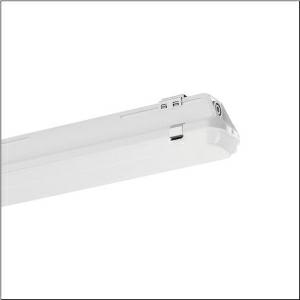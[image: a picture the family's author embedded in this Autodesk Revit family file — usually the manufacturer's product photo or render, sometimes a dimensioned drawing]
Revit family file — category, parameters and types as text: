
# Revit family: monsun_r__21_51fb207p660c005_979b
name_source: partatom
category: Lighting Fixtures
units: mm (PartAtom-declared; Revit-internal decimal feet)

## family parameters
Cut with Voids When Loaded = No
Host = Face
Light Source = No
Part Type = Normal
Room Calculation Point = No
Round Connector Dimension = Use Diameter
Shared = No

## types (1)
- Monsun® 21 (1 x LED, 5410 lm, 34.9 W, 6500K)
    Apparent Load = 35 VA
    CIE Flux Codes = 45 75 93 94 100
    Color Rendering = 80
    Color Temperature = 6500K
    Default Elevation = 1800 mm
    Description = Monsun® 21, damp-proof luminaire, chain hanger, primary optical cover: enclosure, of PC, light emission: direct distribution, primary light characteristic: symmetric, installation type: suspended mounting, surface-mounted, horizontal mounting, vertical mounting, LED, rated luminous flux: 5.410lm, luminous efficacy: 155lm/W, light colour: 865, colour temperature: 6500K, control gear: ON/OFF, with terminal, 3-pole, max. 2.5mm², through-wiring: 5x 2.5mm², mains connection: 220..240V, AC, 50/60Hz, rated input power: 35W, housing, of glass-fibre reinforced polyester, uncoated, bright grey, incl. chain hanger, length: 1.590mm, width: 90mm, height: 88mm, clip for enclosure, of stainless steel (V2A), ceiling mounting element, of stainless steel (V2A), chain hanger, of stainless steel (V2A), protection rating (complete): IP66, insulation class (complete): insulation class I (protective earthing), certification: CE, ENEC, VDE, UKCA, protection symbol: D, impact resistance: IK08, permissible operating ambient temperature: -25..+35°C, standard: EN 50419, EN 60598-2-1, corresponds to IFS (International Featured Standards) requirements for safety and quality in the food industry, for indoor or canopied outdoor use, no direct snow, no direct sun, no direct rain, LABS conformity tested according to VDMA 24364:2018-05, contact your sales advisor before using the luminaires in applications with unclear chemical exposure, large temperature fluctuations or condensation-forming humidity, packaging unit: 1 piece
    Height = 89 mm
    Lamp = 1 x LED
    Lamp Light Flux = 5410 lm
    Lamp Power = 34.9 W
    Lamp count = 1
    Length = 1590 mm
    Luminous efficacy = 155 lm/W
    Manufacturer = Siteco
    ModVariant = No
    Model = 51FB207P660C005
    Mounting Place = Ceiling
    Mounting Type = Surface mounted
    Number of Poles = 1
    OnlyDefault = Yes
    Power Factor = 1
    Product Name = Monsun® 21
    Product group = damp-proof luminaire
    ProductGroupID = 300
    Protection Class = Protection class I
    Protection Degree = IP 66
    RLX_Detail_Level = 1
    RLX_Emergency_Light_Flux = 0 lm
    RLX_Emergency_Type = 0
    RLX_Emergency_Type_DB = No
    RlxData = <blob elided: 88341 chars, md5=fd7bb1ea>
    Socket = socket
    Standby Power = 0 W
    System Light Flux = 5410 lm
    System Power = 35 W
    Type Comments = Product without accessories
    Type Image = l_1319656.jpg
    URL = http://relux.com
    VarID = ---
    Voltage = 0 V
    Weight = 0.00 kg
    Width = 90 mm

## geometry (parser evidence)
native form markers: Blend x4, Sweep x11
no freeform markers — native parametric forms only
